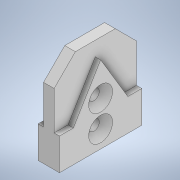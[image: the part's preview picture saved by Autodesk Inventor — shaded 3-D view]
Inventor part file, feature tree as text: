
AUTODESK INVENTOR PART (.ipt)
format: ipt  version: 2022 (Build 260153000, 153)  size: 178,688 bytes
history: native  units: in
note: dims shown in document units (in); Inventor stores cm internally (conversion verified against a paired STEP export)
features: sketch x5, extrude x4, mirror x3, other x3, hole x2, projected_geometry x2, chamfer x1
ambient origin geometry x8: Origin, YZ Plane, XZ Plane, XY Plane, X Axis, Y Axis, Z Axis, Center Point
bodies: Solid1 (feature_tree)
feature tree (20):
  extrude  "Extrusion1"  Depth=0.8858in
  extrude  "Extrusion4"  Depth=0.1575in
  mirror  "Mirror2"
  extrude  "Extrusion5"  Depth=0.0787in TaperAngle=0.0deg
  extrude  "Extrusion6"  Depth=0.3937in TaperAngle=0.0deg
  mirror  "Mirror3"
  mirror  "Mirror4"
  sketch  "Sketch9"  dims[d40=0.1575in d41=0.3937in d42=0.3937in d43=0.1575in d44=0.2362in d45=0.3543in d46=0.0787in d47=90.0deg d48=0.315in d49=0.8108in d50=0.3937in d51=0.3937in d52=0.3937in d53=0.1575in d54=0.2362in d55=0.3543in d56=0.0787in d57=90.0deg d58=0.315in d59=0.8108in d60=0.315in d61=0.0787in d62=45.0deg]
  other  "Work Point4"
  other  "Work Point5"
  hole  "Hole3"  [1 undecoded]
  other  "Work Point6"
  hole  "Hole4"  [1 undecoded]
  chamfer  "Chamfer1"  [1 undecoded]
  sketch  "Sketch1"  dims[d0=1.2205in d1=0.8858in]
  sketch  "Sketch2"  dims[d2=0.1575in d3=0.0in d31=0.8067in]
  sketch  "Sketch7"  dims[d33=0.6723in d34=0.0787in d35=0.0in]
  projected_geometry  "Projected Loop2"
  sketch  "Sketch8"  dims[d36=0.4724in d37=0.0in d38=0.3937in d39=0.0in]
  projected_geometry  "Projected Loop3"
note: 3 required parameter values undecoded (feature->parameter linkage not recoverable at this tier; creation-order binding heuristic only, values carry confidence <= 0.55)
